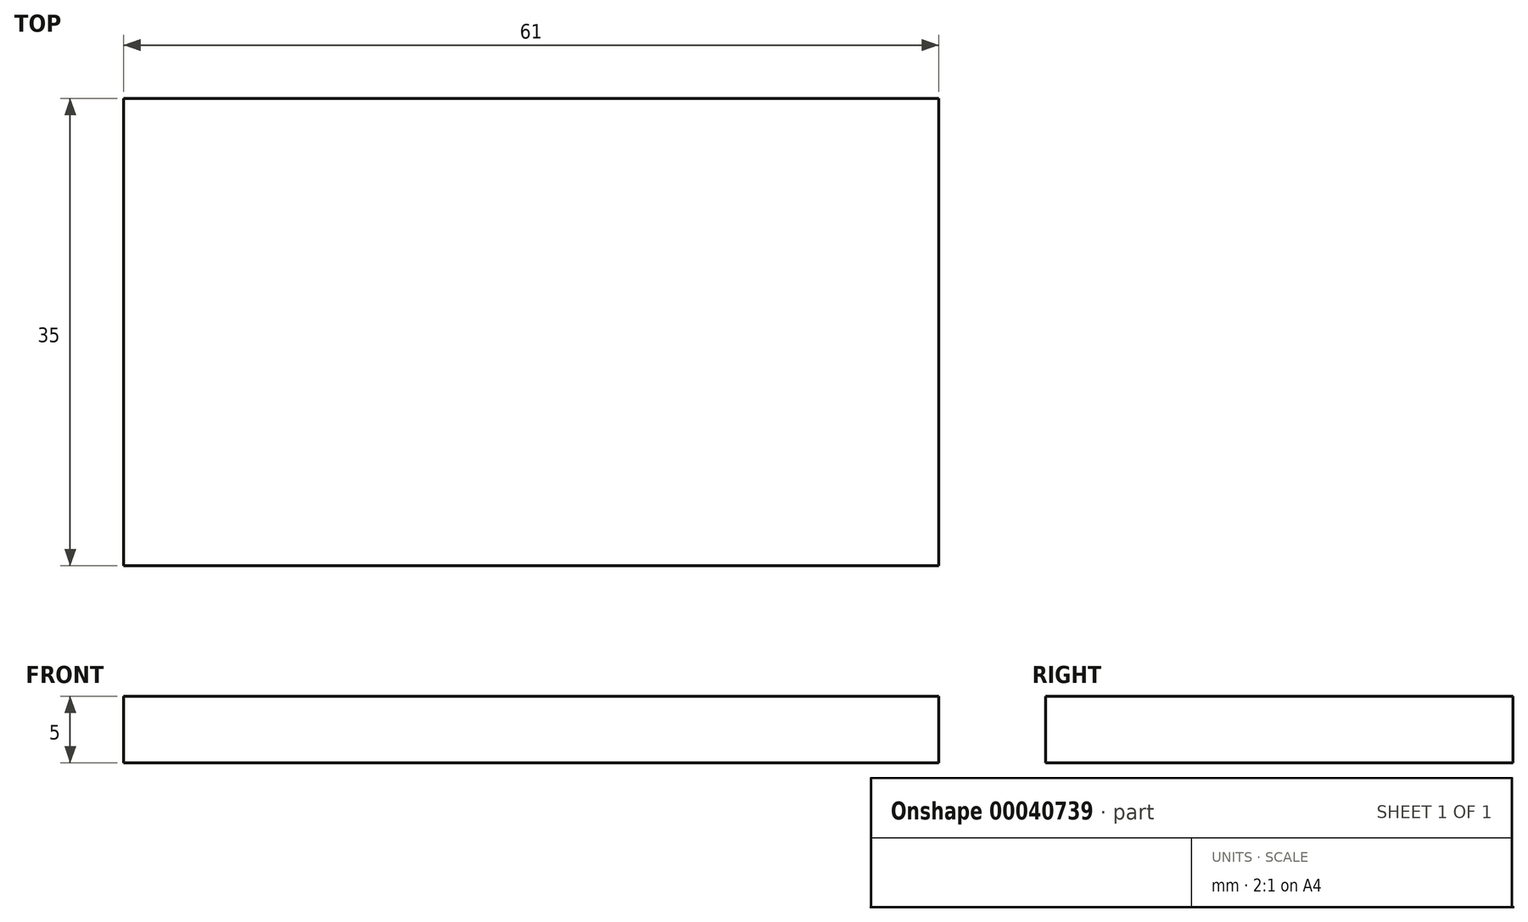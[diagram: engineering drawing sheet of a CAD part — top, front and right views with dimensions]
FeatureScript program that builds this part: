
annotation { "Feature Type Name" : "Feature", "Feature Type Description" : "" }
export const myFeature = defineFeature(function(context is Context, id is Id, definition is map)
    precondition{}
    {
        {
            var Q0;
            Q0=qCreatedBy(makeId("Top.planeOp"),FACE);
            var sketch = newSketch(context, id + "F0", { "sketchPlane" : qUnion([Q0])});
            skLineSegment(sketch, "E0.rect.bottom", {"start": v(30.5, -17.5) * mm, "end": v(-30.5, -17.5) * mm});
            skLineSegment(sketch, "E0.rect.top", {"start": v(30.5, 17.5) * mm, "end": v(-30.5, 17.5) * mm});
            skLineSegment(sketch, "E0.rect.left", {"start": v(30.5, -17.5) * mm, "end": v(30.5, 17.5) * mm});
            skLineSegment(sketch, "E0.rect.right", {"start": v(-30.5, -17.5) * mm, "end": v(-30.5, 17.5) * mm});
            skPoint(sketch, "E0.rect.middle", {"position": v(0, 0) * mm});
            skSolve(sketch);
        }
        {
            var Q0;
            Q0=makeQuery(id+"F0.imprint","IMPRINT",FACE,{"disambiguationData":[TD([[makeQuery(id+"F0.imprint","IMPRINT",EDGE,{"derivedFrom":sQuery(id+"F0.wireOp",EDGE,"E0.rect.bottom")}),-1.0]])]});
            extrude(context, id + "F1", {"entities" : qUnion([Q0]), "depth" : 5 * mm});
        }
    });
